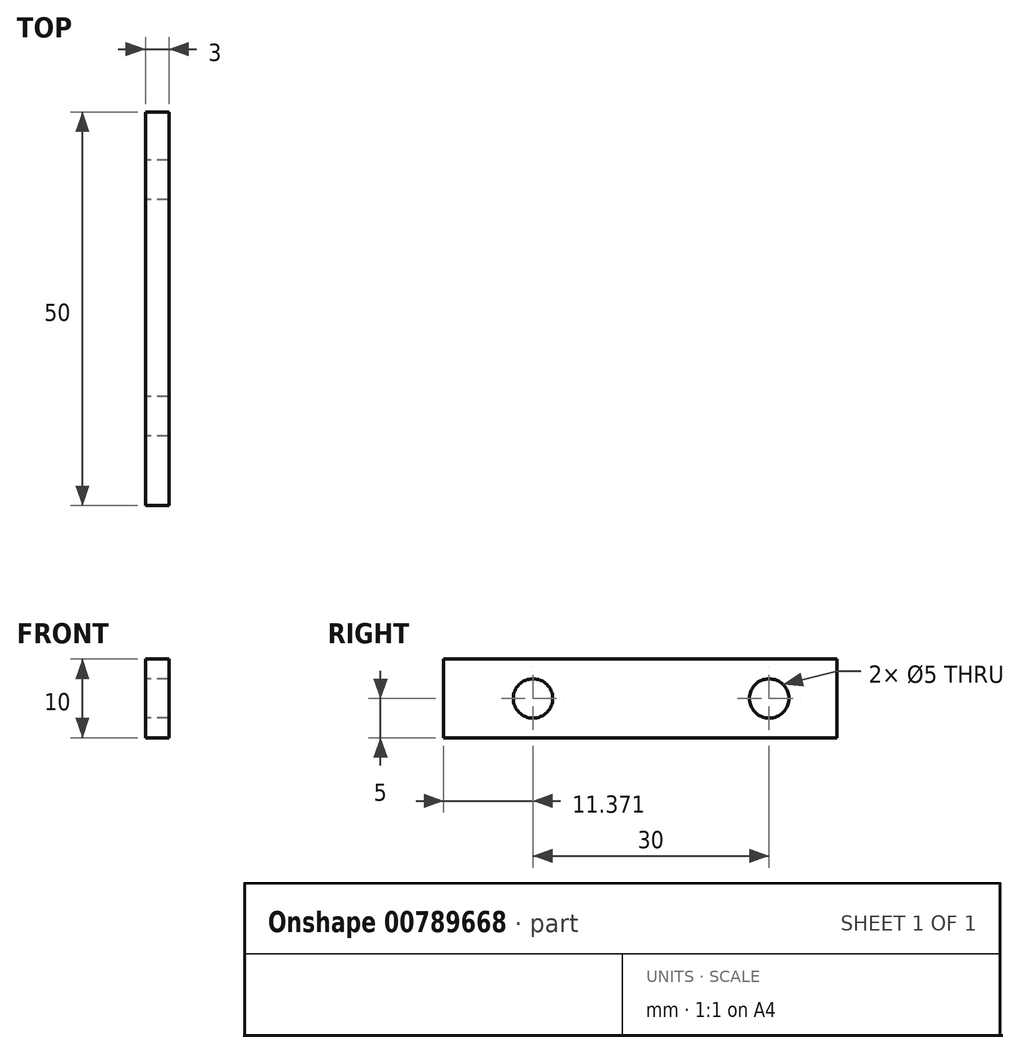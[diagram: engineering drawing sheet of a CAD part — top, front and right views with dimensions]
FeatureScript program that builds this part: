
annotation { "Feature Type Name" : "Feature", "Feature Type Description" : "" }
export const myFeature = defineFeature(function(context is Context, id is Id, definition is map)
    precondition{}
    {
        {
            var Q0;
            Q0=qCreatedBy(makeId("Right.planeOp"),FACE);
            var sketch = newSketch(context, id + "F0", { "sketchPlane" : qUnion([Q0])});
            skLineSegment(sketch, "E0.bottom", {"start": v(-50, 10) * mm, "end": v(0, 10) * mm});
            skLineSegment(sketch, "E0.top", {"start": v(-50, 0) * mm, "end": v(0, 0) * mm});
            skLineSegment(sketch, "E0.left", {"start": v(-50, 10) * mm, "end": v(-50, 0) * mm});
            skLineSegment(sketch, "E0.right", {"start": v(0, 10) * mm, "end": v(0, 0) * mm});
            skCircle(sketch, "E1", {"center": v(-8.63, 5) * mm, "radius": 2.5 * mm});
            skPoint(sketch, "E1.centerSnap0", {"position": v(0, 5) * mm});
            skCircle(sketch, "E2", {"center": v(-38.63, 5) * mm, "radius": 2.5 * mm});
            skPoint(sketch, "E2.centerSnap0", {"position": v(-50, 5) * mm});
            skSolve(sketch);
        }
        {
            var Q0;
            Q0=makeQuery(id+"F0.imprint","IMPRINT",FACE,{"disambiguationData":[TD([[makeQuery(id+"F0.imprint","IMPRINT",EDGE,{"derivedFrom":sQuery(id+"F0.wireOp",EDGE,"E0.bottom")}),-1.0]])]});
            extrude(context, id + "F1", {"entities" : qUnion([Q0]), "depth" : 5 * mm, "offsetDistance" : 25 * mm});
        }
        {
            var Q0;
            Q0=makeQuery(id+"F1.opExtrude","CAP_FACE",FACE,{"disambiguationData":[OSD([sQuery(id+"F0.wireOp",EDGE,"E0.bottom"),sQuery(id+"F0.wireOp",EDGE,"E0.top"),sQuery(id+"F0.wireOp",EDGE,"E0.left"),sQuery(id+"F0.wireOp",EDGE,"E0.right"),sQuery(id+"F0.wireOp",EDGE,"E1"),sQuery(id+"F0.wireOp",EDGE,"E2")])],"isStart":false});
            extrude(context, id + "F2", {"entities" : qUnion([Q0]), "operationType" : NewBodyOperationType.REMOVE, "oppositeDirection" : true, "depth" : 2 * mm, "offsetDistance" : 25 * mm});
        }
    });
